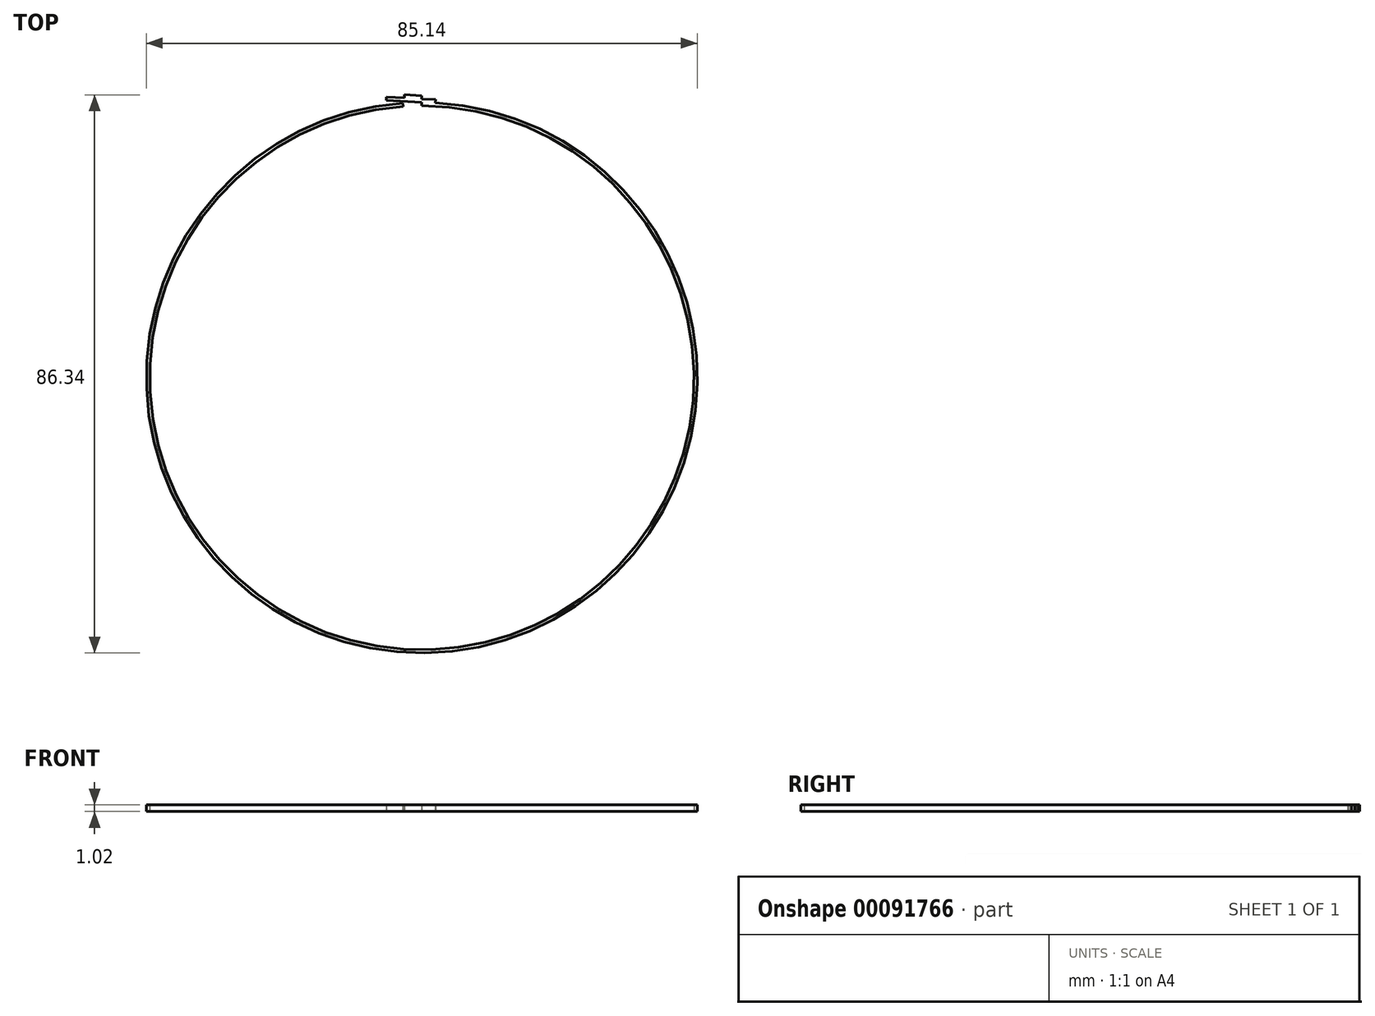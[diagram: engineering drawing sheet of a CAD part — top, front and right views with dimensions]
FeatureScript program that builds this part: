
annotation { "Feature Type Name" : "Feature", "Feature Type Description" : "" }
export const myFeature = defineFeature(function(context is Context, id is Id, definition is map)
    precondition{}
    {
        {
            var Q0;
            Q0=qCreatedBy(makeId("Top.planeOp"),FACE);
            var sketch = newSketch(context, id + "F0", { "sketchPlane" : qUnion([Q0])});
            skArc(sketch, "E0", {"start": v(-5.84, 41.66) * mm, "mid": v(-27.6, -31.74) * mm, "end": v(42.06, 0) * mm});
            skArc(sketch, "E1", {"start": v(-2.92, 42.47) * mm, "mid": v(0.41, -42.57) * mm, "end": v(2.1, 42.52) * mm});
            skLineSegment(sketch, "E2", {"start": v(-5.9, 42.16) * mm, "end": v(-5.98, 42.66) * mm});
            skLineSegment(sketch, "E3.trimOffspring", {"start": v(2.1, 42.52) * mm, "end": v(2.12, 43.03) * mm});
            skArc(sketch, "E4", {"start": v(42.06, 0) * mm, "mid": v(29.74, 29.74) * mm, "end": v(0, 42.06) * mm});
            skLineSegment(sketch, "E5", {"start": v(2.12, 43.03) * mm, "end": v(0, 43.13) * mm});
            skLineSegment(sketch, "E6", {"start": v(-5.5, 43.4) * mm, "end": v(-5.5, 42.9) * mm});
            skLineSegment(sketch, "E7", {"start": v(-5.5, 42.9) * mm, "end": v(0, 42.62) * mm});
            skLineSegment(sketch, "E8", {"start": v(-2.92, 42.47) * mm, "end": v(-2.88, 41.96) * mm});
            skPoint(sketch, "E9.start.orphan", {"position": v(0, 42.06) * mm});
            skArc(sketch, "E10.trimOffspring", {"start": v(-2.88, 41.96) * mm, "mid": v(-4.36, 41.84) * mm, "end": v(-5.84, 41.66) * mm});
            skLineSegment(sketch, "E11", {"start": v(0, 42.06) * mm, "end": v(0, 42.62) * mm});
            skLineSegment(sketch, "E12", {"start": v(0, 43.13) * mm, "end": v(0, 43.64) * mm});
            skLineSegment(sketch, "E13", {"start": v(0, 43.64) * mm, "end": v(-2.7, 43.77) * mm});
            skLineSegment(sketch, "E14", {"start": v(-2.7, 43.77) * mm, "end": v(-2.72, 43.27) * mm});
            skLineSegment(sketch, "E15.trimOffspring", {"start": v(-2.72, 43.27) * mm, "end": v(-5.5, 43.4) * mm});
            skSolve(sketch);
        }
        {
            var Q0;
            Q0 = qSketchRegion(id + "F0", true);
            extrude(context, id + "F1", {"entities" : qUnion([Q0]), "flatOperationType" : FlatOperationType.REMOVE, "offsetDistance" : 25.4 * mm, "depth" : 1.02 * mm, "domain" : OperationDomain.MODEL});
        }
    });
